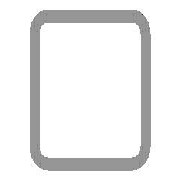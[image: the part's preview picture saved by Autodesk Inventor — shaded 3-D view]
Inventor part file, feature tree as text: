
AUTODESK INVENTOR PART (.ipt)
format: ipt  version: 2025 (Build 290162010, 162A)  size: 164,864 bytes
history: native  units: mm (DEFAULTED — no unit token found)
features: other x4, sketch x2, extrude x1, pattern_circular x1, plane x1
ambient origin geometry x8: Origin, YZ Plane, XZ Plane, XY Plane, X Axis, Y Axis, Z Axis, Center Point
bodies: Solid1 (feature_tree), Body (feature_tree)
feature tree (9):
  parser-record x1  (decoder bookkeeping rows leaked as tree rows — omitted from the tree; the rows remain in map.json)
  other  "Driven Length"
  other  "Start Plane"
  other  "End Plane"
  extrude  "Extrusion2"  TaperAngle=0.0deg  [1 undecoded]
  pattern_circular  "Circular Pattern1"  Count=4  [1 undecoded]
  sketch  "Sketch3"  dims[d3=2500.0mm d4=0.0mm]
  plane  "Work Plane3"
  sketch  "Sketch5"  dims[d7=4.0mm d9=40.0mm d11=40.0mm d12=2.0mm d13=-0.0mm d14=2500.0mm d15=20.0mm d16=20.0mm d17=90.0deg d18=2500.0mm d19=5.5mm d21=50.0mm d22=50.0mm d23=50.0mm d25=25.0mm d26=0.0mm d27=0.0mm d28=20.0mm d29=90.0deg]
note: 2 required parameter values undecoded (feature->parameter linkage not recoverable at this tier; creation-order binding heuristic only, values carry confidence <= 0.55)
